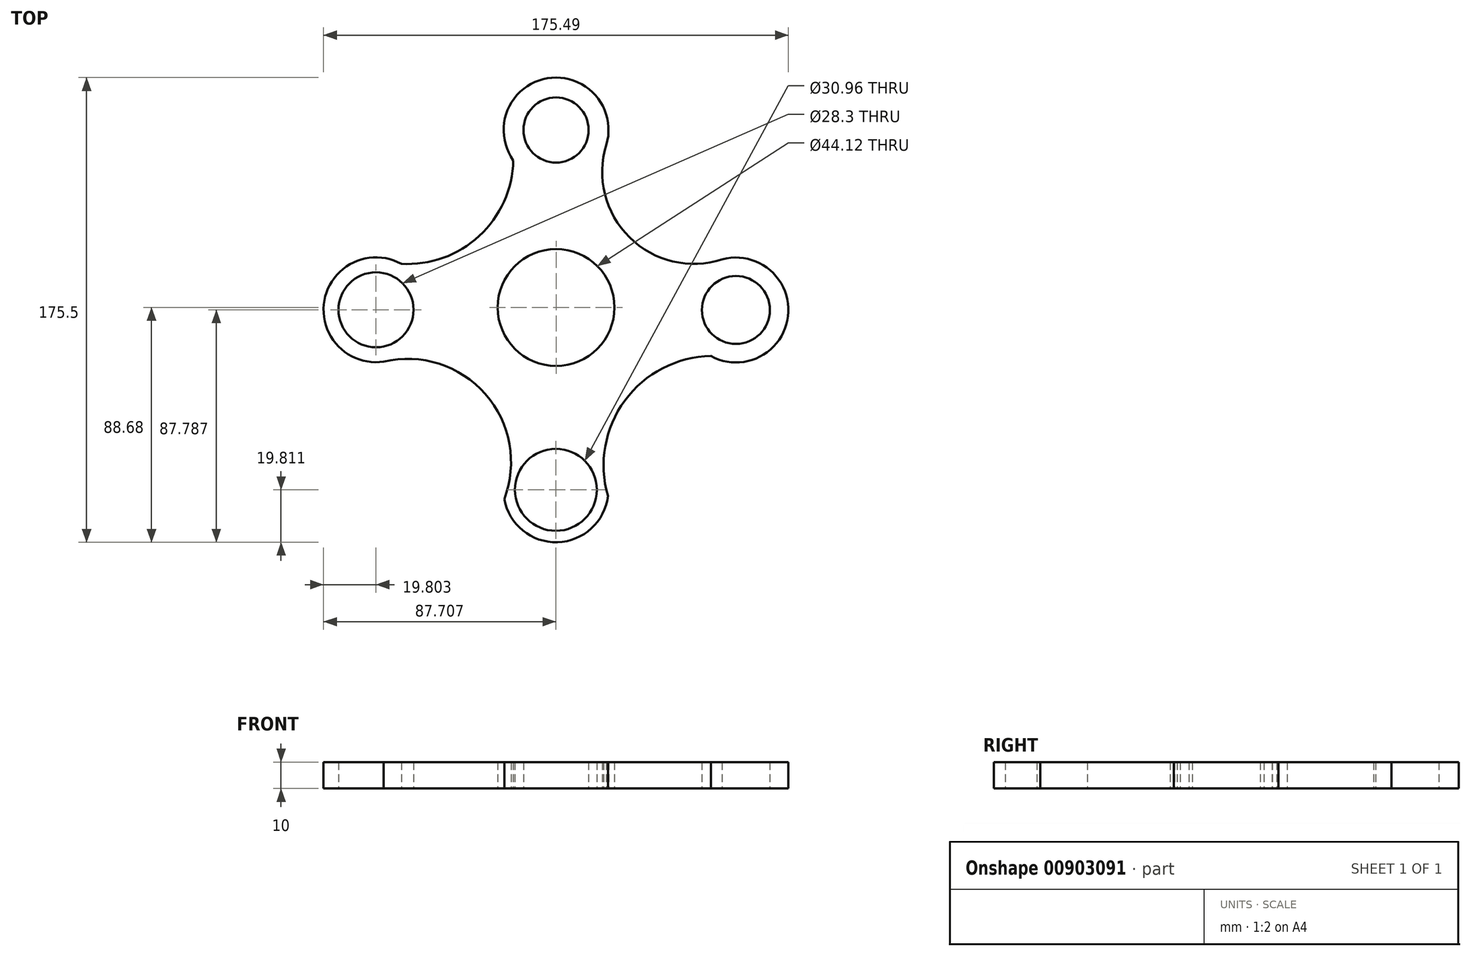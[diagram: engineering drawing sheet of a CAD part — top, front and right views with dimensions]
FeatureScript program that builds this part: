
annotation { "Feature Type Name" : "Feature", "Feature Type Description" : "" }
export const myFeature = defineFeature(function(context is Context, id is Id, definition is map)
    precondition{}
    {
        {
            var Q0;
            Q0=qCreatedBy(makeId("Top.planeOp"),FACE);
            var sketch = newSketch(context, id + "F0", { "sketchPlane" : qUnion([Q0])});
            skCircle(sketch, "E0", {"center": v(0, 0) * mm, "radius": 22.06 * mm});
            skArc(sketch, "E1", {"start": v(19, 61.42) * mm, "mid": v(-3.27, 86.54) * mm, "end": v(-16.14, 55.53) * mm});
            skCircle(sketch, "E2", {"center": v(0, -62.13) * mm, "radius": 2 * mm});
            skArc(sketch, "E3.1.0", {"start": v(-58.43, 16.46) * mm, "mid": v(-87.47, 2.6) * mm, "end": v(-65.06, -20.48) * mm});
            skArc(sketch, "E3.2.0", {"start": v(-19.57, -72.36) * mm, "mid": v(0.52, -88.67) * mm, "end": v(19.6, -71.18) * mm});
            skArc(sketch, "E3.3.0", {"start": v(58.43, -18.36) * mm, "mid": v(87.57, -3.28) * mm, "end": v(62.72, 18.15) * mm});
            skPoint(sketch, "E3.center", {"position": v(-0.04, -0.93) * mm});
            skCircle(sketch, "E4", {"center": v(-67.98, -0.9) * mm, "radius": 14.15 * mm});
            skCircle(sketch, "E5", {"center": v(0, 67.01) * mm, "radius": 12.3 * mm});
            skCircle(sketch, "E6", {"center": v(-0.07, -68.87) * mm, "radius": 15.48 * mm});
            skCircle(sketch, "E7", {"center": v(67.9, -0.97) * mm, "radius": 12.82 * mm});
            skArc(sketch, "E8", {"start": v(-58.43, 16.46) * mm, "mid": v(-28.99, 27.02) * mm, "end": v(-16.14, 55.53) * mm});
            skArc(sketch, "E9", {"start": v(19, 61.42) * mm, "mid": v(27.7, 26.5) * mm, "end": v(62.72, 18.15) * mm});
            skArc(sketch, "E10", {"start": v(-19.57, -72.36) * mm, "mid": v(-26.68, -32.72) * mm, "end": v(-65.06, -20.48) * mm});
            skArc(sketch, "E11", {"start": v(58.43, -18.36) * mm, "mid": v(25.96, -35.17) * mm, "end": v(19.6, -71.18) * mm});
            skSolve(sketch);
        }
        {
            var Q0;
            Q0=makeQuery(id+"F0.imprint","IMPRINT",FACE,{"disambiguationData":[TD([[makeQuery(id+"F0.imprint","IMPRINT",EDGE,{"derivedFrom":sQuery(id+"F0.wireOp",EDGE,"E0")}),-1.0]])]});
            var sketch = newSketch(context, id + "F1", { "sketchPlane" : qUnion([Q0])});
            skSolve(sketch);
        }
        {
            var Q0;
            Q0 = qSketchRegion(id + "F1", true);
            var Q1;
            Q1=makeQuery(id+"F1.imprint","IMPRINT",FACE,{"disambiguationData":[TD([[makeQuery(id+"F1.imprint","IMPRINT",EDGE,{"derivedFrom":makeQuery(id+"F0.imprint","IMPRINT",EDGE,{"derivedFrom":sQuery(id+"F0.wireOp",EDGE,"E0")})}),-1.0]])]});
            extrude(context, id + "F2", {"entities" : qUnion([Q0, Q1]), "depth" : 10 * mm, "offsetDistance" : 25 * mm});
        }
    });
